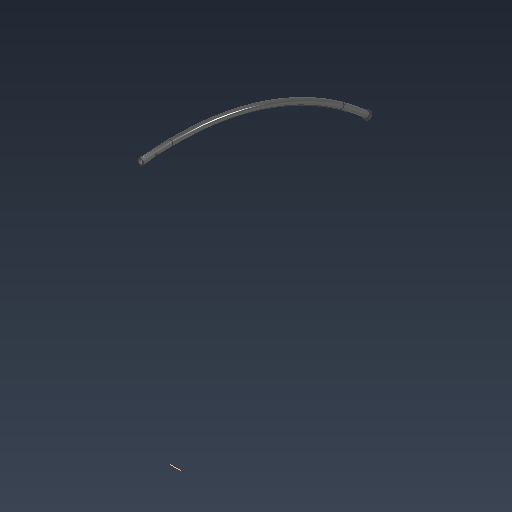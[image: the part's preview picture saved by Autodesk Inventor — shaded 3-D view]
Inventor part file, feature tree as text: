
AUTODESK INVENTOR PART (.ipt)
format: ipt  version: 2021 (Build 250183000, 183)  size: 2,193,920 bytes
history: native  units: mm
features: sketch x10, extrude x8, sweep x2, fillet x2, plane x2, split x2, pattern_circular x1
ambient origin geometry x8: Origin, YZ Plane, XZ Plane, XY Plane, X Axis, Y Axis, Z Axis, Center Point
bodies: Solid1 (feature_tree), Solid2 (feature_tree), Solid3 (feature_tree), Solid6 (feature_tree), Solid7 (feature_tree)
feature tree (27):
  sketch  "Sketch1"  dims[d0=3300.0mm d1=1650.0mm]
  sweep  "Sweep1"
  sweep  "Sweep2"
  extrude  "Extrusion1"  Depth=27.3mm
  extrude  "Extrusion3"  Depth=1650.0mm
  pattern_circular  "Circular Pattern1"  Count=120  [1 undecoded]
  extrude  "Extrusion5"  Depth=1701.0mm
  fillet  "Fillet1"  Radius=200.0mm
  sketch  "Sketch11"  dims[d12=3402.0mm]
  extrude  "Extrusion7"  TaperAngle=0.0deg  [1 undecoded]
  extrude  "Extrusion8"  Depth=10.0mm
  extrude  "Extrusion9"  Depth=10.0mm
  extrude  "Extrusion10"  Depth=0.5mm
  extrude  "Extrusion11"  Depth=1.0mm
  fillet  "Fillet3"  Radius=10.0mm
  plane  "Work Plane2"
  split  "Split1"
  plane  "Work Plane4"
  split  "Split3"
  sketch  "Sketch2"  dims[d2=0.0mm d3=33.7mm]
  sketch  "Sketch3"  dims[d4=0.0mm d5=0.0mm d6=27.3mm]
  sketch  "Sketch4"  dims[d7=0.0mm d8=1650.0mm]
  sketch  "Sketch5"  dims[d9=0.0mm d10=0.0mm]
  sketch  "Sketch9"  dims[d11=1752.0mm]
  sketch  "Sketch12"  dims[d13=1701.0mm d14=1200.0mm]
  sketch  "Sketch13"  dims[d15=1701.0mm d16=1701.0mm d17=200.0mm]
  sketch  "Sketch14"  dims[d18=51.0mm d19=0.0mm d20=19.0mm d21=19.0mm d22=0.5mm d25=1.0mm d26=10.0mm d27=0.0mm d28=680.0mm d29=7.679449mm d38=10.0mm d39=5.0mm d40=10.0mm d41=0.0mm d42=2.0mm d45=2.0mm d46=3300.0mm d47=100.0mm d48=0.0mm d50=10.0mm d51=0.0mm d52=10.0mm d53=12.0mm d54=0.0mm d56=10.0mm d57=0.0mm d58=3300.0mm d59=8.0mm d60=100.0mm d61=0.0mm d62=3.2mm d63=5.0mm d64=2.0mm d65=-200.0mm d67=-170.0mm]
note: 2 required parameter values undecoded (feature->parameter linkage not recoverable at this tier; creation-order binding heuristic only, values carry confidence <= 0.55)
